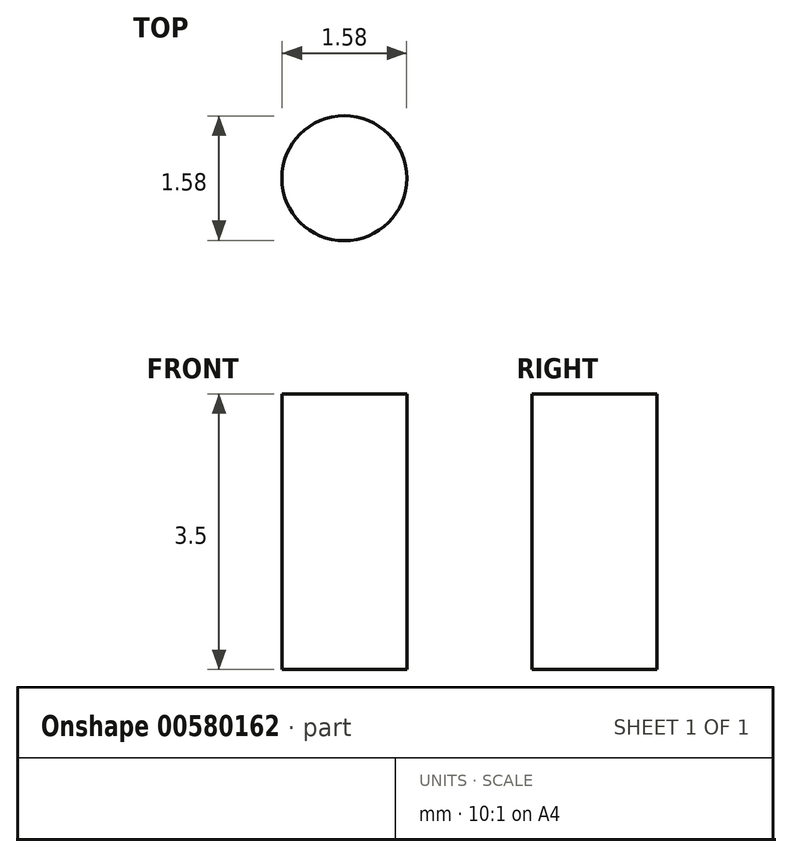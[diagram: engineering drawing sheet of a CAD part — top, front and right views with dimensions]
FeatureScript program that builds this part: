
annotation { "Feature Type Name" : "Feature", "Feature Type Description" : "" }
export const myFeature = defineFeature(function(context is Context, id is Id, definition is map)
    precondition{}
    {
        {
            var Q0;
            Q0=qCreatedBy(makeId("Top.planeOp"),FACE);
            var sketch = newSketch(context, id + "F0", { "sketchPlane" : qUnion([Q0])});
            skCircle(sketch, "E0", {"center": v(0, 0) * mm, "radius": 0.8 * mm});
            skSolve(sketch);
        }
        {
            var Q0;
            Q0 = qSketchRegion(id + "F0", true);
            extrude(context, id + "F1", {"entities" : qUnion([Q0]), "depth" : 3.5 * mm, "offsetDistance" : 25 * mm});
        }
    });
